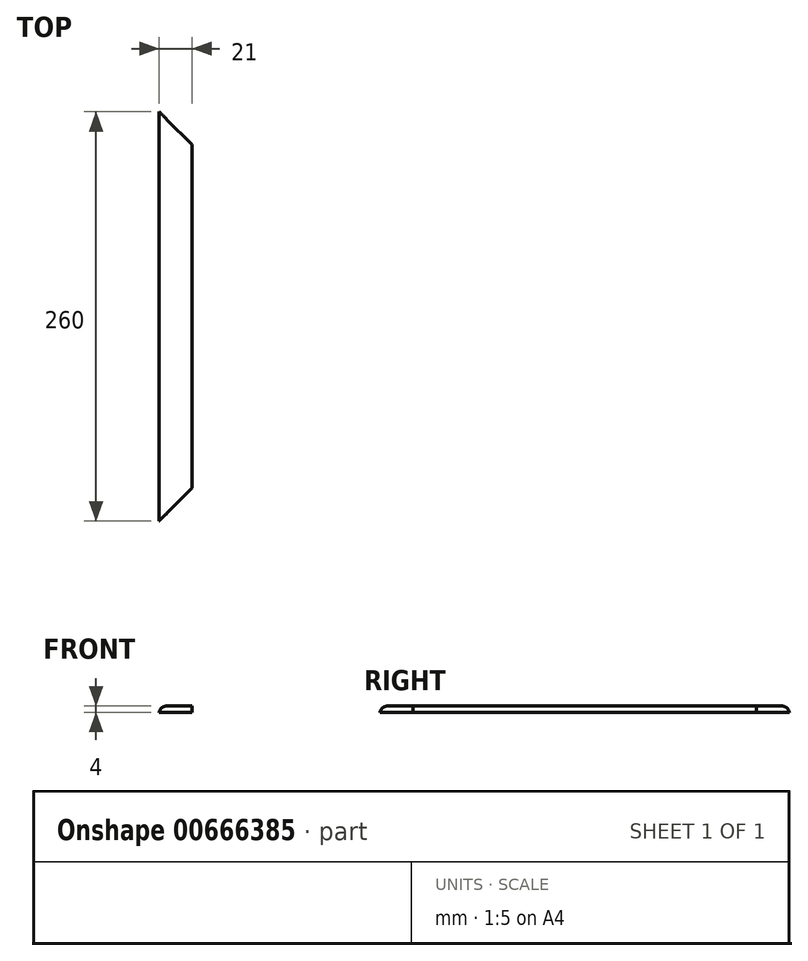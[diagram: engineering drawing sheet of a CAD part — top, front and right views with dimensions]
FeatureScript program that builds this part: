
annotation { "Feature Type Name" : "Feature", "Feature Type Description" : "" }
export const myFeature = defineFeature(function(context is Context, id is Id, definition is map)
    precondition{}
    {
        {
            var Q0;
            Q0=qCreatedBy(makeId("Top.planeOp"),FACE);
            var sketch = newSketch(context, id + "F0", { "sketchPlane" : qUnion([Q0])});
            skLineSegment(sketch, "E0.bottom", {"start": v(10.5, 130) * mm, "end": v(-10.5, 130) * mm});
            skLineSegment(sketch, "E0.top", {"start": v(10.5, -130) * mm, "end": v(-10.5, -130) * mm});
            skLineSegment(sketch, "E0.left", {"start": v(10.5, 130) * mm, "end": v(10.5, -130) * mm});
            skLineSegment(sketch, "E0.right", {"start": v(-10.5, 130) * mm, "end": v(-10.5, -130) * mm});
            skPoint(sketch, "E0.middle", {"position": v(0, 0) * mm});
            skSolve(sketch);
        }
        {
            var Q0;
            Q0 = qSketchRegion(id + "F0", true);
            extrude(context, id + "F1", {"entities" : qUnion([Q0]), "depth" : 4 * mm, "offsetDistance" : 25 * mm});
        }
        {
            var Q0;
            Q0=makeQuery(id+"F1.opExtrude","CAP_FACE",FACE,{"disambiguationData":[OSD([sQuery(id+"F0.wireOp",EDGE,"E0.bottom"),sQuery(id+"F0.wireOp",EDGE,"E0.top"),sQuery(id+"F0.wireOp",EDGE,"E0.left"),sQuery(id+"F0.wireOp",EDGE,"E0.right")])],"isStart":false});
            var sketch = newSketch(context, id + "F2", { "sketchPlane" : qUnion([Q0])});
            skLineSegment(sketch, "E1", {"start": v(-10.5, 130) * mm, "end": v(10.5, 109) * mm});
            skLineSegment(sketch, "E2", {"start": v(10.5, 109) * mm, "end": v(10.5, 130) * mm});
            skLineSegment(sketch, "E3", {"start": v(10.5, 130) * mm, "end": v(-10.5, 130) * mm});
            skLineSegment(sketch, "E4", {"start": v(-10.5, -130) * mm, "end": v(10.5, -109) * mm});
            skLineSegment(sketch, "E5", {"start": v(10.5, -109) * mm, "end": v(10.5, -130) * mm});
            skLineSegment(sketch, "E6", {"start": v(10.5, -130) * mm, "end": v(-10.5, -130) * mm});
            skSolve(sketch);
        }
        {
            var Q0;
            Q0 = qSketchRegion(id + "F2", true);
            extrude(context, id + "F3", {"entities" : qUnion([Q0]), "operationType" : NewBodyOperationType.REMOVE, "endBound" : BoundingType.THROUGH_ALL, "oppositeDirection" : true, "depth" : 25 * mm, "offsetDistance" : 25 * mm});
        }
        {
            var Q0;
            Q0=makeQuery(id+"F1.opExtrude","CAP_EDGE",EDGE,{"disambiguationData":[OSD([sQuery(id+"F0.wireOp",EDGE,"E0.right")])],"isStart":false});
            fillet(context, id + "F4", {"entities" : qUnion([Q0]), "radius" : 5 * mm, "tangentPropagation" : true, "allowEdgeOverflow" : false});
        }
    });
